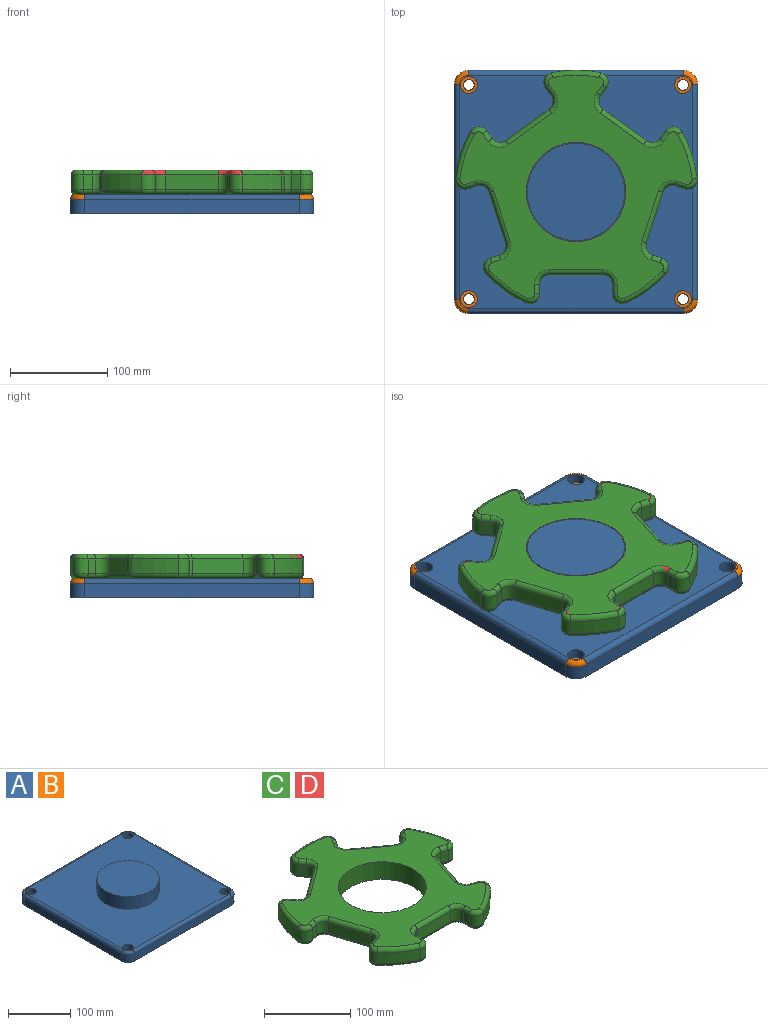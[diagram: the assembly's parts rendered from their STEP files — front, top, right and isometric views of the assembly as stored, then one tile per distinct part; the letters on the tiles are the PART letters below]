
ASSEMBLY  parts=4 mates=1
PART A: 32 faces, bbox 252.5x252.5x45 mm
  f0: plane 220x15mm, normal (1,0,0), area 3300mm2, adj f5,f8,f11,f27
  f1: plane 220x15mm, normal (0,1,0), area 3300mm2, adj f5,f8,f9,f31
  f2: plane 220x15mm, normal (-1,0,0), area 3300mm2, adj f5,f9,f10,f28
  f3: plane 220x15mm, normal (0,-1,0), area 3300mm2, adj f5,f10,f11,f24
  f4: plane 240x240mm, normal (0,0,1), area 48725.4mm2, adj f6,f14,f17,f20,f23,f24,f25,f26
  f5: plane 250x250mm, normal (0,0,-1), area 61926.7mm2, adj f0,f1,f2,f3,f8,f9,f10,f11
  f6: cylinder r=50mm len=100mm, axis (0,0,-1), area 7854mm2, adj f4,f7
  f7: plane 100x100mm, normal (0,0,1), area 7854mm2, adj f6
  f8: cylinder r=15mm len=15mm, axis (0,0,-1), area 353.4mm2, adj f0,f1,f5,f29
  f9: cylinder r=15mm len=15mm, axis (0,0,1), area 353.4mm2, adj f1,f2,f5,f30
  f10: cylinder r=15mm len=15mm, axis (0,0,-1), area 353.4mm2, adj f2,f3,f5,f26
  f11: cylinder r=15mm len=15mm, axis (0,0,1), area 353.4mm2, adj f0,f3,f5,f25
  f12: cylinder r=5.5mm len=11mm, axis (0,0,1), area 345.6mm2, adj f5,f13
  f13: plane 17.25x17.25mm, normal (0,0,1), area 138.7mm2, adj f12,f14
  f14: cylinder r=8.62mm len=17.25mm, axis (0,0,1), area 541.9mm2, adj f4,f13
  f15: cylinder r=5.5mm len=11mm, axis (0,0,1), area 345.6mm2, adj f5,f16
  f16: plane 17.25x17.25mm, normal (0,0,1), area 138.7mm2, adj f15,f17
  f17: cylinder r=8.62mm len=17.25mm, axis (0,0,1), area 541.9mm2, adj f4,f16
  f18: cylinder r=5.5mm len=11mm, axis (0,0,1), area 345.6mm2, adj f5,f19
  f19: plane 17.25x17.25mm, normal (0,0,1), area 138.7mm2, adj f18,f20
  f20: cylinder r=8.62mm len=17.25mm, axis (0,0,1), area 541.9mm2, adj f4,f19
  f21: cylinder r=5.5mm len=11mm, axis (0,0,1), area 345.6mm2, adj f5,f22
  f22: plane 17.25x17.25mm, normal (0,0,1), area 138.7mm2, adj f21,f23
  f23: cylinder r=8.62mm len=17.25mm, axis (0,0,1), area 541.9mm2, adj f4,f22
  f24: cylinder r=5mm len=220mm, axis (-1,0,0), area 1727.9mm2, adj f3,f4,f25,f26
  f25: torus R=10mm, axis (0,0,1), area 162.6mm2, adj f4,f11,f24,f27
  f26: torus R=10mm, axis (0,0,1), area 162.6mm2, adj f4,f10,f24,f28
  f27: cylinder r=5mm len=220mm, axis (0,-1,0), area 1727.9mm2, adj f0,f4,f25,f29
  f28: cylinder r=5mm len=220mm, axis (0,1,0), area 1727.9mm2, adj f2,f4,f26,f30
  f29: torus R=10mm, axis (0,0,1), area 162.6mm2, adj f4,f8,f27,f31
  f30: torus R=10mm, axis (0,0,1), area 162.6mm2, adj f4,f9,f28,f31
  f31: cylinder r=5mm len=220mm, axis (1,0,0), area 1727.9mm2, adj f1,f4,f29,f30
PART B: same geometry as A
PART C: 123 faces, bbox 268.9x258.5x25 mm
  f0: plane 238.57x229.73mm, normal (0,0,1), area 21505.7mm2, adj f6,f43,f44,f45,f46,f47,f48,f49
  f1: plane 238.57x229.73mm, normal (0,0,-1), area 21505.7mm2, adj f6,f83,f84,f85,f86,f87,f88,f89
  f2: cylinder r=125mm len=40.68mm, axis (0,0,-1), area 759.5mm2, adj f13,f42,f51,f91
  f3: cylinder r=125mm len=47.82mm, axis (0,0,-1), area 759.5mm2, adj f35,f41,f67,f107
  f4: cylinder r=125mm len=50.29mm, axis (0,0,-1), area 759.5mm2, adj f28,f34,f82,f122
  f5: cylinder r=125mm len=47.82mm, axis (0,0,-1), area 759.5mm2, adj f21,f27,f66,f106
  f6: cylinder r=51mm len=102mm, axis (0,0,-1), area 8011.1mm2, adj f0,f1
  f7: cylinder r=125mm len=40.68mm, axis (0,0,-1), area 759.5mm2, adj f14,f20,f50,f90
  f8: plane 15x9.73mm, normal (-1,0,0), area 146mm2, adj f11,f14,f46,f86
  f9: plane 55x15mm, normal (0,-1,0), area 825mm2, adj f11,f12,f43,f83
  f10: plane 15x9.73mm, normal (1,0,0), area 146mm2, adj f12,f13,f47,f87
  f11: cylinder r=10mm len=15mm, axis (0,0,-1), area 235.6mm2, adj f8,f9,f44,f84
  f12: cylinder r=10mm len=15mm, axis (0,0,-1), area 235.6mm2, adj f9,f10,f45,f85
  f13: cylinder r=10mm len=15mm, axis (0,0,-1), area 299.5mm2, adj f2,f10,f49,f89
  f14: cylinder r=10mm len=15mm, axis (0,0,-1), area 299.5mm2, adj f7,f8,f48,f88
  f15: plane 15x9.26mm, normal (-0.31,-0.95,0), area 146mm2, adj f18,f21,f62,f102
  f16: plane 52.31x17mm, normal (0.95,-0.31,0), area 825mm2, adj f18,f19,f58,f98
  f17: plane 15x9.26mm, normal (0.31,0.95,0), area 146mm2, adj f19,f20,f54,f94
  f18: cylinder r=10mm len=15mm, axis (0,0,-1), area 235.6mm2, adj f15,f16,f60,f100
  f19: cylinder r=10mm len=15mm, axis (0,0,-1), area 235.6mm2, adj f16,f17,f56,f96
  f20: cylinder r=10mm len=16.25mm, axis (0,0,-1), area 299.5mm2, adj f7,f17,f52,f92
  f21: cylinder r=10mm len=15mm, axis (0,0,-1), area 299.5mm2, adj f5,f15,f64,f104
  f22: plane 15x7.87mm, normal (0.81,-0.59,0), area 146mm2, adj f25,f28,f78,f118
  f23: plane 44.5x32.33mm, normal (0.59,0.81,0), area 825mm2, adj f25,f26,f74,f114
  f24: plane 15x7.87mm, normal (-0.81,0.59,0), area 146mm2, adj f26,f27,f70,f110
  f25: cylinder r=10mm len=15mm, axis (0,0,-1), area 235.6mm2, adj f22,f23,f76,f116
  f26: cylinder r=10mm len=15mm, axis (0,0,-1), area 235.6mm2, adj f23,f24,f72,f112
  f27: cylinder r=10mm len=16.78mm, axis (0,0,-1), area 299.5mm2, adj f5,f24,f68,f108
  f28: cylinder r=10mm len=15.67mm, axis (0,0,-1), area 299.5mm2, adj f4,f22,f80,f120
  f29: plane 15x7.87mm, normal (0.81,0.59,0), area 146mm2, adj f32,f35,f71,f111
  f30: plane 44.5x32.33mm, normal (-0.59,0.81,0), area 825mm2, adj f32,f33,f75,f115
  f31: plane 15x7.87mm, normal (-0.81,-0.59,0), area 146mm2, adj f33,f34,f79,f119
  f32: cylinder r=10mm len=15mm, axis (0,0,-1), area 235.6mm2, adj f29,f30,f73,f113
  f33: cylinder r=10mm len=15mm, axis (0,0,-1), area 235.6mm2, adj f30,f31,f77,f117
  f34: cylinder r=10mm len=15.67mm, axis (0,0,-1), area 299.5mm2, adj f4,f31,f81,f121
  f35: cylinder r=10mm len=16.78mm, axis (0,0,-1), area 299.5mm2, adj f3,f29,f69,f109
  f36: plane 15x9.26mm, normal (-0.31,0.95,0), area 146mm2, adj f39,f42,f55,f95
  f37: plane 52.31x17mm, normal (-0.95,-0.31,0), area 825mm2, adj f39,f40,f59,f99
  f38: plane 15x9.26mm, normal (0.31,-0.95,0), area 146mm2, adj f40,f41,f63,f103
  f39: cylinder r=10mm len=15mm, axis (0,0,-1), area 235.6mm2, adj f36,f37,f57,f97
  f40: cylinder r=10mm len=15mm, axis (0,0,-1), area 235.6mm2, adj f37,f38,f61,f101
  f41: cylinder r=10mm len=15mm, axis (0,0,-1), area 299.5mm2, adj f3,f38,f65,f105
  f42: cylinder r=10mm len=16.25mm, axis (0,0,-1), area 299.5mm2, adj f2,f36,f53,f93
  f43: cylinder r=5mm len=55mm, axis (1,0,0), area 432mm2, adj f0,f9,f44,f45
  f44: torus R=15mm, axis (0,0,1), area 145.8mm2, adj f0,f11,f43,f46
  f45: torus R=15mm, axis (0,0,1), area 145.8mm2, adj f0,f12,f43,f47
  f46: cylinder r=5mm len=9.73mm, axis (0,-1,0), area 76.4mm2, adj f0,f8,f44,f48
  f47: cylinder r=5mm len=9.73mm, axis (0,1,0), area 76.4mm2, adj f0,f10,f45,f49
  f48: torus R=5mm, axis (0,0,1), area 128.3mm2, adj f0,f14,f46,f50
  f49: torus R=5mm, axis (0,0,1), area 128.3mm2, adj f0,f13,f47,f51
  f50: torus R=120mm, axis (0,0,1), area 391.9mm2, adj f0,f7,f48,f52
  f51: torus R=120mm, axis (0,0,1), area 391.9mm2, adj f0,f2,f49,f53
  f52: torus R=5mm, axis (0,0,1), area 128.3mm2, adj f0,f20,f50,f54
  f53: torus R=5mm, axis (0,0,1), area 128.3mm2, adj f0,f42,f51,f55
  f54: cylinder r=5mm len=10.8mm, axis (-0.95,0.31,0), area 76.4mm2, adj f0,f17,f52,f56
  f55: cylinder r=5mm len=10.8mm, axis (-0.95,-0.31,0), area 76.4mm2, adj f0,f36,f53,f57
  f56: torus R=15mm, axis (0,0,1), area 145.8mm2, adj f0,f19,f54,f58
  f57: torus R=15mm, axis (0,0,1), area 145.8mm2, adj f0,f39,f55,f59
  f58: cylinder r=5mm len=53.85mm, axis (0.31,0.95,0), area 432mm2, adj f0,f16,f56,f60
  f59: cylinder r=5mm len=53.85mm, axis (0.31,-0.95,0), area 432mm2, adj f0,f37,f57,f61
  f60: torus R=15mm, axis (0,0,1), area 145.8mm2, adj f0,f18,f58,f62
  f61: torus R=15mm, axis (0,0,1), area 145.8mm2, adj f0,f40,f59,f63
  f62: cylinder r=5mm len=10.8mm, axis (0.95,-0.31,0), area 76.4mm2, adj f0,f15,f60,f64
  f63: cylinder r=5mm len=10.8mm, axis (0.95,0.31,0), area 76.4mm2, adj f0,f38,f61,f65
  f64: torus R=5mm, axis (0,0,1), area 128.3mm2, adj f0,f21,f62,f66
  f65: torus R=5mm, axis (0,0,1), area 128.3mm2, adj f0,f41,f63,f67
  f66: torus R=120mm, axis (0,0,1), area 391.9mm2, adj f0,f5,f64,f68
  f67: torus R=120mm, axis (0,0,1), area 391.9mm2, adj f0,f3,f65,f69
  f68: torus R=5mm, axis (0,0,1), area 128.3mm2, adj f0,f27,f66,f70
  f69: torus R=5mm, axis (0,0,1), area 128.3mm2, adj f0,f35,f67,f71
  f70: cylinder r=5mm len=10.81mm, axis (-0.59,-0.81,0), area 76.4mm2, adj f0,f24,f68,f72
  f71: cylinder r=5mm len=10.81mm, axis (-0.59,0.81,0), area 76.4mm2, adj f0,f29,f69,f73
  f72: torus R=15mm, axis (0,0,1), area 145.8mm2, adj f0,f26,f70,f74
  f73: torus R=15mm, axis (0,0,1), area 145.8mm2, adj f0,f32,f71,f75
  f74: cylinder r=5mm len=47.44mm, axis (-0.81,0.59,0), area 432mm2, adj f0,f23,f72,f76
  f75: cylinder r=5mm len=47.44mm, axis (-0.81,-0.59,0), area 432mm2, adj f0,f30,f73,f77
  f76: torus R=15mm, axis (0,0,1), area 145.8mm2, adj f0,f25,f74,f78
  f77: torus R=15mm, axis (0,0,1), area 145.8mm2, adj f0,f33,f75,f79
  f78: cylinder r=5mm len=10.81mm, axis (0.59,0.81,0), area 76.4mm2, adj f0,f22,f76,f80
  f79: cylinder r=5mm len=10.81mm, axis (0.59,-0.81,0), area 76.4mm2, adj f0,f31,f77,f81
  f80: torus R=5mm, axis (0,0,1), area 128.3mm2, adj f0,f28,f78,f82
  f81: torus R=5mm, axis (0,0,1), area 128.3mm2, adj f0,f34,f79,f82
  f82: torus R=120mm, axis (0,0,1), area 391.9mm2, adj f0,f4,f80,f81
  f83: cylinder r=5mm len=55mm, axis (-1,0,0), area 432mm2, adj f1,f9,f84,f85
  f84: torus R=15mm, axis (0,0,1), area 145.8mm2, adj f1,f11,f83,f86
  f85: torus R=15mm, axis (0,0,1), area 145.8mm2, adj f1,f12,f83,f87
  f86: cylinder r=5mm len=9.73mm, axis (0,1,0), area 76.4mm2, adj f1,f8,f84,f88
  f87: cylinder r=5mm len=9.73mm, axis (0,-1,0), area 76.4mm2, adj f1,f10,f85,f89
  f88: torus R=5mm, axis (0,0,1), area 128.3mm2, adj f1,f14,f86,f90
  f89: torus R=5mm, axis (0,0,1), area 128.3mm2, adj f1,f13,f87,f91
  f90: torus R=120mm, axis (0,0,1), area 391.9mm2, adj f1,f7,f88,f92
  f91: torus R=120mm, axis (0,0,1), area 391.9mm2, adj f1,f2,f89,f93
  f92: torus R=5mm, axis (0,0,1), area 128.3mm2, adj f1,f20,f90,f94
  f93: torus R=5mm, axis (0,0,1), area 128.3mm2, adj f1,f42,f91,f95
  f94: cylinder r=5mm len=10.8mm, axis (0.95,-0.31,0), area 76.4mm2, adj f1,f17,f92,f96
  f95: cylinder r=5mm len=10.8mm, axis (0.95,0.31,0), area 76.4mm2, adj f1,f36,f93,f97
  f96: torus R=15mm, axis (0,0,1), area 145.8mm2, adj f1,f19,f94,f98
  f97: torus R=15mm, axis (0,0,1), area 145.8mm2, adj f1,f39,f95,f99
  f98: cylinder r=5mm len=53.85mm, axis (-0.31,-0.95,0), area 432mm2, adj f1,f16,f96,f100
  f99: cylinder r=5mm len=53.85mm, axis (-0.31,0.95,0), area 432mm2, adj f1,f37,f97,f101
  f100: torus R=15mm, axis (0,0,1), area 145.8mm2, adj f1,f18,f98,f102
  f101: torus R=15mm, axis (0,0,1), area 145.8mm2, adj f1,f40,f99,f103
  f102: cylinder r=5mm len=10.8mm, axis (-0.95,0.31,0), area 76.4mm2, adj f1,f15,f100,f104
  f103: cylinder r=5mm len=10.8mm, axis (-0.95,-0.31,0), area 76.4mm2, adj f1,f38,f101,f105
  f104: torus R=5mm, axis (0,0,1), area 128.3mm2, adj f1,f21,f102,f106
  f105: torus R=5mm, axis (0,0,1), area 128.3mm2, adj f1,f41,f103,f107
  f106: torus R=120mm, axis (0,0,1), area 391.9mm2, adj f1,f5,f104,f108
  f107: torus R=120mm, axis (0,0,1), area 391.9mm2, adj f1,f3,f105,f109
  f108: torus R=5mm, axis (0,0,1), area 128.3mm2, adj f1,f27,f106,f110
  f109: torus R=5mm, axis (0,0,1), area 128.3mm2, adj f1,f35,f107,f111
  f110: cylinder r=5mm len=10.81mm, axis (0.59,0.81,0), area 76.4mm2, adj f1,f24,f108,f112
  f111: cylinder r=5mm len=10.81mm, axis (0.59,-0.81,0), area 76.4mm2, adj f1,f29,f109,f113
  f112: torus R=15mm, axis (0,0,1), area 145.8mm2, adj f1,f26,f110,f114
  f113: torus R=15mm, axis (0,0,1), area 145.8mm2, adj f1,f32,f111,f115
  f114: cylinder r=5mm len=47.44mm, axis (0.81,-0.59,0), area 432mm2, adj f1,f23,f112,f116
  f115: cylinder r=5mm len=47.44mm, axis (0.81,0.59,0), area 432mm2, adj f1,f30,f113,f117
  f116: torus R=15mm, axis (0,0,1), area 145.8mm2, adj f1,f25,f114,f118
  f117: torus R=15mm, axis (0,0,1), area 145.8mm2, adj f1,f33,f115,f119
  f118: cylinder r=5mm len=10.81mm, axis (-0.59,-0.81,0), area 76.4mm2, adj f1,f22,f116,f120
  f119: cylinder r=5mm len=10.81mm, axis (-0.59,0.81,0), area 76.4mm2, adj f1,f31,f117,f121
  f120: torus R=5mm, axis (0,0,1), area 128.3mm2, adj f1,f28,f118,f122
  f121: torus R=5mm, axis (0,0,1), area 128.3mm2, adj f1,f34,f119,f122
  f122: torus R=120mm, axis (0,0,1), area 391.9mm2, adj f1,f4,f120,f121
PART D: same geometry as C
PLACE A at identity
PLACE B at identity
PLACE C at identity
PLACE D at identity
MATE revolute B.f6 <-> C.f2  axis (0,0,1) through (0,0,45)mm
